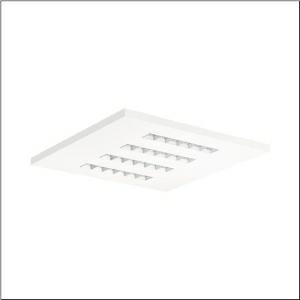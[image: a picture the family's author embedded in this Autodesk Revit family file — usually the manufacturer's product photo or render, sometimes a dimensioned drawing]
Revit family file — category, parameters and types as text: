
# Revit family: silica_r__21_square_51mx6mdu44w_c9d7
name_source: partatom
category: Lighting Fixtures
units: mm (PartAtom-declared; Revit-internal decimal feet)

## family parameters
Cut with Voids When Loaded = No
Host = Face
Light Source = No
Part Type = Normal
Room Calculation Point = No
Round Connector Dimension = Use Diameter
Shared = No

## types (1)
- --- (1 x LED, 4600 lm, 27.2 W, 4000K)
    Apparent Load = 27 VA
    CIE Flux Codes = 83 98 100 100 100
    Color Rendering = 80
    Color Temperature = 4000K
    Default Elevation = 1800 mm
    Description = Silica® 21 Square, office luminaire, primary light control with lens, of PMMA, primary anti-glare with reflector, of PC, white, CAT 2 (L<= 3000cd/m²), light emission: direct distribution, primary light characteristic: symmetric, installation type: lay-in mounting, LED, rated luminous flux: 4.600lm, luminous efficacy: 169lm/W, light colour: 840, colour temperature: 4000K, control gear: DALI 2, with terminal, 5-pole, mains connection: 220..240V, AC, 50/60Hz, rated input power: 27.2W, luminaire housing, of sheet steel, coated, traffic white (RAL 9016), module: M625, length: 622mm, width: 622mm, height: 33mm, protection rating (complete): IP20, insulation class (complete): insulation class I (protective earthing), certification: CE, ENEC, VDE, permissible operating ambient temperature: -20..+40°C, standard: EN 50419, packaging unit: 1 piece
    Height = 0 mm  [stored 0 ft]
    Lamp = 1 x LED
    Lamp Light Flux = 4600 lm
    Lamp Power = 27.2 W
    Lamp count = 1
    Length = 622 mm
    Luminous efficacy = 169 lm/W
    Manufacturer = Siteco
    ModVariant = No
    Model = 51MX6MDU44W
    Mounting Place = Ceiling
    Mounting Type = Recessed
    Number of Poles = 1
    OnlyDefault = Yes
    Power Factor = 1
    Product Name = Silica® 21 Square
    Product group = office luminaire | ceiling recessed
    ProductGroupID = 401
    Protection Class = Protection class I
    Protection Degree = IP 20
    RLX_Detail_Level = 1
    RLX_Emergency_Light_Flux = 0 lm
    RLX_Emergency_Type = 0
    RLX_Emergency_Type_DB = No
    RlxData = <blob elided: 18637 chars, md5=b02d156a>
    Socket = socket
    Standby Power = 0 W
    System Light Flux = 4600 lm
    System Power = 27 W
    Type Comments = factory setting: luminous flux: 100 % | dim-lin: 254 | 366 mA
    Type Image = l_1275220.jpg
    URL = http://relux.com
    VarID = @adj_083698
    Voltage = 0 V
    Weight = 0.00 kg
    Width = 622 mm

note: [stored X ft] marks values corroborated as IEEE doubles in the binary element streams (Revit-internal decimal feet)

## geometry (parser evidence)
native form markers: Blend x4, Sweep x11
no freeform markers — native parametric forms only
